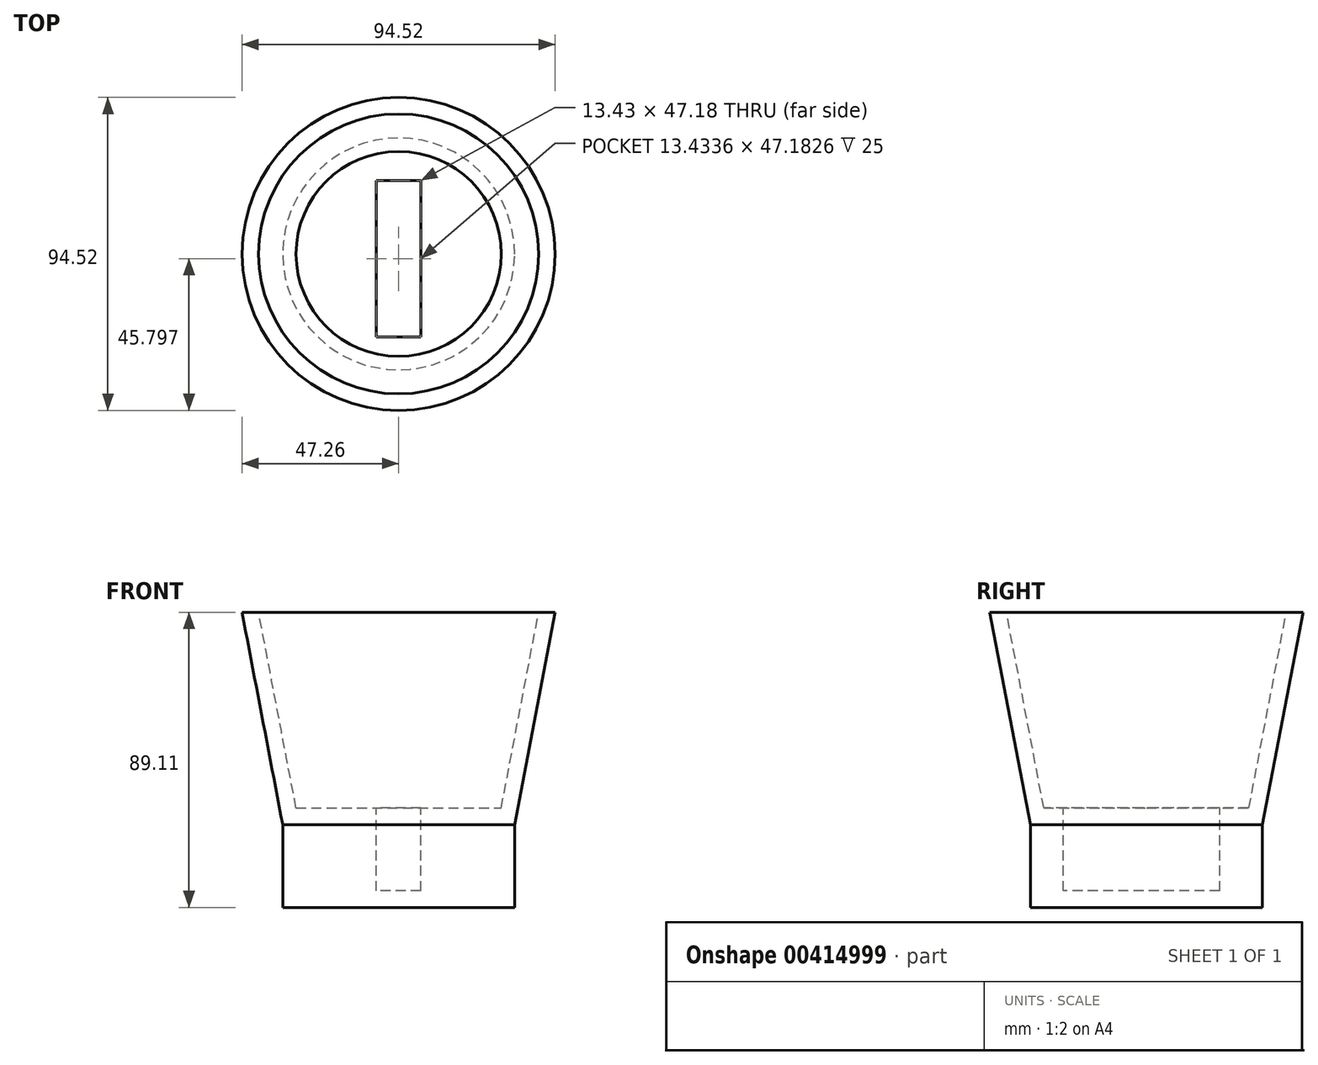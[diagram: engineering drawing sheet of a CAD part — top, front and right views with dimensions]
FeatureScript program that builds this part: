
annotation { "Feature Type Name" : "Feature", "Feature Type Description" : "" }
export const myFeature = defineFeature(function(context is Context, id is Id, definition is map)
    precondition{}
    {
        {
            var Q0;
            Q0=qCreatedBy(makeId("Front.planeOp"),FACE);
            var sketch = newSketch(context, id + "F0", { "sketchPlane" : qUnion([Q0])});
            skLineSegment(sketch, "E0", {"start": v(-47.26, 64.11) * mm, "end": v(-35, 0) * mm});
            skLineSegment(sketch, "E1", {"start": v(-47.26, 64.11) * mm, "end": v(-42.26, 64.11) * mm});
            skLineSegment(sketch, "E2", {"start": v(0, 0) * mm, "end": v(0, 5) * mm});
            skLineSegment(sketch, "E3", {"start": v(-42.26, 64.11) * mm, "end": v(-30.96, 5) * mm});
            skLineSegment(sketch, "E4", {"start": v(0, 5) * mm, "end": v(-30.96, 5) * mm});
            skLineSegment(sketch, "E5", {"start": v(-35, 0) * mm, "end": v(-35, -25) * mm});
            skLineSegment(sketch, "E6", {"start": v(-35, -25) * mm, "end": v(0, -25) * mm});
            skLineSegment(sketch, "E7", {"start": v(0, -25) * mm, "end": v(0, 0) * mm});
            skSolve(sketch);
        }
        {
            var Q0;
            Q0=makeQuery(id+"F0.imprint","IMPRINT",FACE,{"disambiguationData":[TD([[makeQuery(id+"F0.imprint","IMPRINT",EDGE,{"derivedFrom":sQuery(id+"F0.wireOp",EDGE,"E0")}),1.0]])]});
            var Q1;
            Q1=sQuery(id+"F0.wireOp",EDGE,"E7");
            revolve(context, id + "F1", {"entities" : qUnion([Q0]), "axis" : qUnion([Q1]), "revolveType" : RevolveType.FULL});
        }
        {
            var Q0;
            Q0=makeQuery(id+"F1.opRevolve","SWEPT_FACE",FACE,{"disambiguationData":[OSD([sQuery(id+"F0.wireOp",EDGE,"E4")])]});
            var sketch = newSketch(context, id + "F2", { "sketchPlane" : qUnion([Q0])});
            skLineSegment(sketch, "E8.bottom", {"start": v(6.72, 22.13) * mm, "end": v(-6.72, 22.13) * mm});
            skLineSegment(sketch, "E8.top", {"start": v(6.72, -25.05) * mm, "end": v(-6.72, -25.05) * mm});
            skLineSegment(sketch, "E8.left", {"start": v(6.72, 22.13) * mm, "end": v(6.72, -25.05) * mm});
            skLineSegment(sketch, "E8.right", {"start": v(-6.72, 22.13) * mm, "end": v(-6.72, -25.05) * mm});
            skPoint(sketch, "E8.middle", {"position": v(0, -1.46) * mm});
            skSolve(sketch);
        }
        {
            var Q0;
            Q0=makeQuery(id+"F2.imprint","IMPRINT",FACE,{"disambiguationData":[TD([[makeQuery(id+"F2.imprint","IMPRINT",EDGE,{"derivedFrom":sQuery(id+"F2.wireOp",EDGE,"E8.bottom")}),1.0]])]});
            extrude(context, id + "F3", {"entities" : qUnion([Q0]), "operationType" : NewBodyOperationType.REMOVE, "oppositeDirection" : true, "depth" : 25 * mm});
        }
    });
